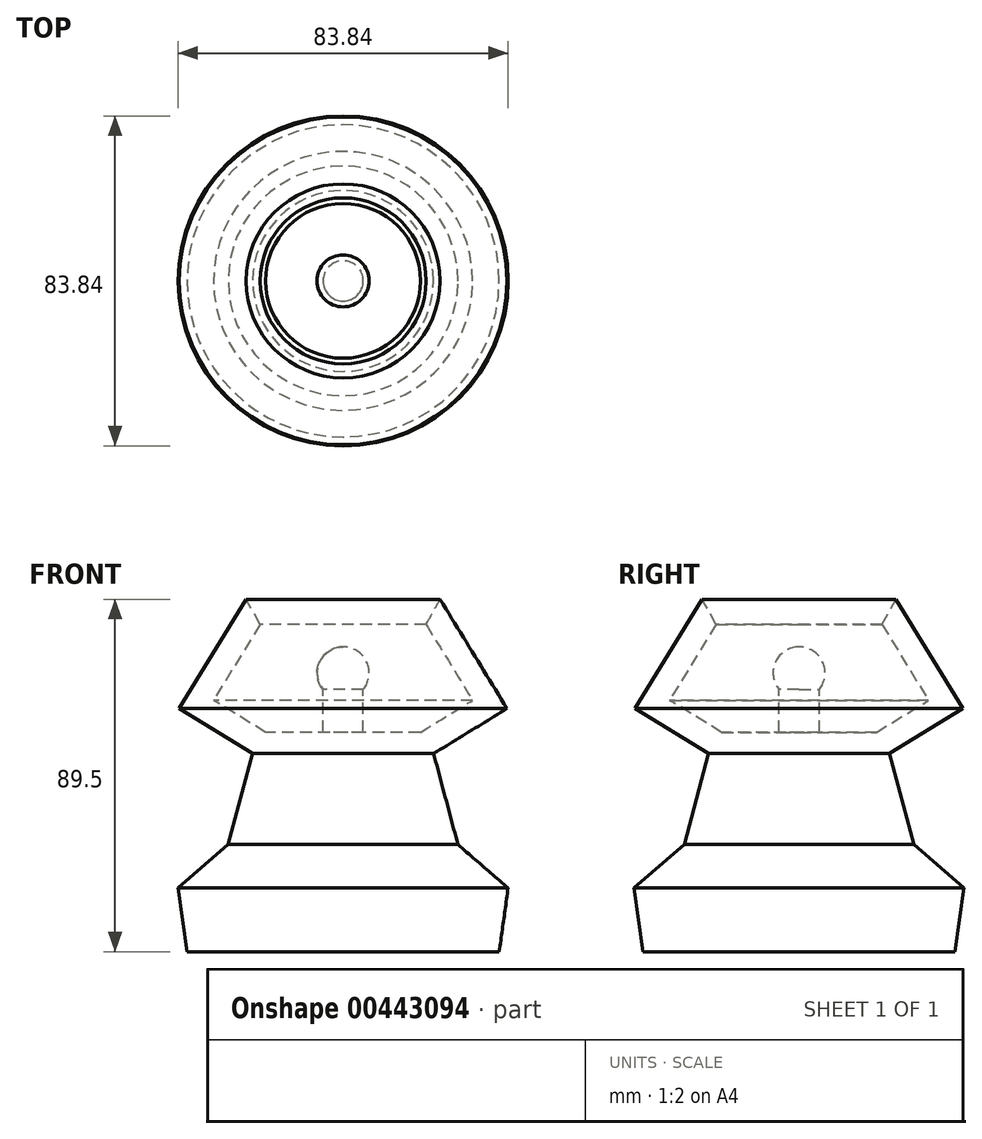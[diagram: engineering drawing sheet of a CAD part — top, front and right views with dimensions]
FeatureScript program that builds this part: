
annotation { "Feature Type Name" : "Feature", "Feature Type Description" : "" }
export const myFeature = defineFeature(function(context is Context, id is Id, definition is map)
    precondition{}
    {
        {
            var Q0;
            Q0=qCreatedBy(makeId("Front.planeOp"),FACE);
            var sketch = newSketch(context, id + "F0", { "sketchPlane" : qUnion([Q0])});
            skLineSegment(sketch, "E0", {"start": v(-24.64, 55.37) * mm, "end": v(-41.64, 27.61) * mm});
            skLineSegment(sketch, "E1", {"start": v(-41.64, 27.61) * mm, "end": v(-22.98, 16.2) * mm});
            skLineSegment(sketch, "E2", {"start": v(-22.98, 16.2) * mm, "end": v(-29.17, -6.94) * mm});
            skLineSegment(sketch, "E3", {"start": v(0, 13.74) * mm, "end": v(0, -6.09) * mm});
            skPoint(sketch, "E4.end.orphan", {"position": v(37.39, 0) * mm});
            skLineSegment(sketch, "E5", {"start": v(-29.17, -6.94) * mm, "end": v(-41.92, -17.98) * mm});
            skLineSegment(sketch, "E6", {"start": v(-41.92, -17.98) * mm, "end": v(-39.65, -34.13) * mm});
            skLineSegment(sketch, "E7", {"start": v(0, -34.13) * mm, "end": v(0, -18.25) * mm});
            skLineSegment(sketch, "E8", {"start": v(-39.65, -34.13) * mm, "end": v(0, -34.13) * mm});
            skPoint(sketch, "E9.orphan", {"position": v(0, -46.3) * mm});
            skLineSegment(sketch, "E10.1", {"start": v(-21.08, 49.02) * mm, "end": v(-32.9, 29.71) * mm});
            skLineSegment(sketch, "E10.2", {"start": v(-32.9, 29.71) * mm, "end": v(-19.67, 21.6) * mm});
            skLineSegment(sketch, "E11", {"start": v(-19.67, 21.6) * mm, "end": v(0, 21.6) * mm});
            skPoint(sketch, "E12.orphan", {"position": v(0, 24.94) * mm});
            skPoint(sketch, "E13.end.orphan", {"position": v(0, 55.37) * mm});
            skLineSegment(sketch, "E14", {"start": v(-24.64, 55.37) * mm, "end": v(-21.08, 49.02) * mm});
            skArc(sketch, "E15", {"start": v(0, 43.29) * mm, "mid": v(-6.61, 36.68) * mm, "end": v(0, 30.07) * mm});
            skLineSegment(sketch, "E16", {"start": v(-5.11, 32.48) * mm, "end": v(-5.11, 21.6) * mm});
            skLineSegment(sketch, "E17", {"start": v(0, 43.29) * mm, "end": v(0, 21.6) * mm});
            skLineSegment(sketch, "E18", {"start": v(-29.17, -6.94) * mm, "end": v(0, -6.09) * mm});
            skLineSegment(sketch, "E19", {"start": v(0, 21.6) * mm, "end": v(0, -6.09) * mm});
            skLineSegment(sketch, "E20", {"start": v(0, -18.25) * mm, "end": v(0, -6.09) * mm});
            skSolve(sketch);
        }
        {
            var Q0;
            Q0=makeQuery(id+"F0.imprint","IMPRINT",FACE,{"disambiguationData":[TD([[makeQuery(id+"F0.imprint","IMPRINT",EDGE,{"derivedFrom":sQuery(id+"F0.wireOp",EDGE,"E0")}),1.0]])]});
            var Q1;
            {var subQ3=sQuery(id+"F0.wireOp",EDGE,"E16");Q1=makeQuery(id+"F0.imprint","IMPRINT",FACE,{"disambiguationData":[TD([[makeQuery(id+"F0.imprint","IMPRINT",EDGE,{"derivedFrom":subQ3}),1.0]])]});}
            var Q2;
            {var subQ0=sQuery(id+"F0.wireOp",EDGE,"E17");var subQ1=sQuery(id+"F0.wireOp",EDGE,"E15");var subQ2=makeQuery(id+"F0.imprint","INTERSECT",VERTEX,{"disambiguationData":[OD(0.0)],"derivedFrom":[subQ1,subQ0]});Q2=makeQuery(id+"F0.imprint","IMPRINT",FACE,{"disambiguationData":[TD([[makeQuery(id+"F0.imprint","IMPRINT",EDGE,{"disambiguationData":[TD([[subQ2,-1.0]])],"derivedFrom":subQ1}),1.0]])]});}
            var Q3;
            Q3=makeQuery(id+"F0.imprint","IMPRINT",FACE,{"disambiguationData":[TD([[makeQuery(id+"F0.imprint","IMPRINT",EDGE,{"derivedFrom":sQuery(id+"F0.wireOp",EDGE,"E5")}),1.0]])]});
            var Q4;
            Q4=sQuery(id+"F0.wireOp",EDGE,"E3");
            revolve(context, id + "F1", {"entities" : qUnion([Q0, Q1, Q2, Q3]), "axis" : qUnion([Q4]), "revolveType" : RevolveType.FULL});
        }
    });
